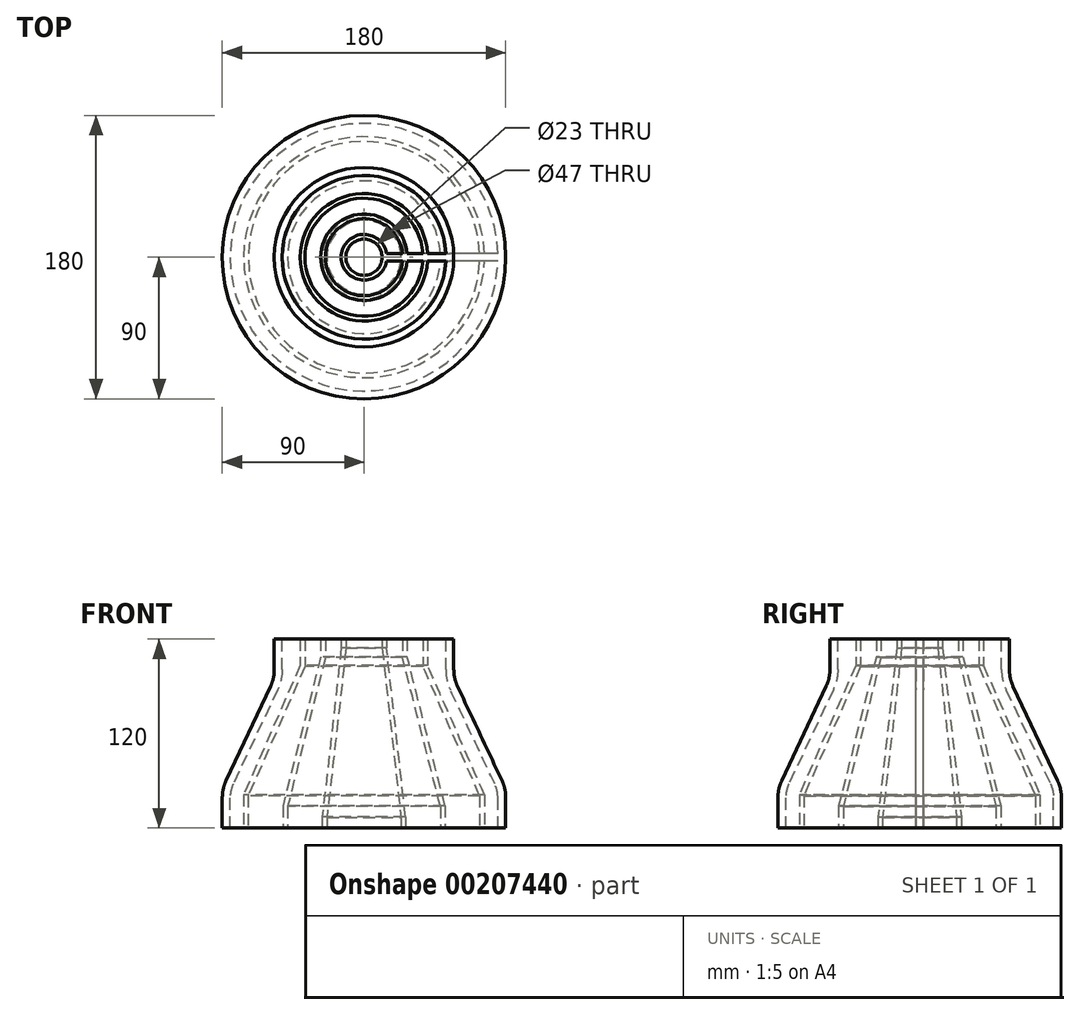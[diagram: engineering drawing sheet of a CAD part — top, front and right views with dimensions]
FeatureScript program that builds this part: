
annotation { "Feature Type Name" : "Feature", "Feature Type Description" : "" }
export const myFeature = defineFeature(function(context is Context, id is Id, definition is map)
    precondition{}
    {
        {
            var Q0;
            Q0=qCreatedBy(makeId("Front.planeOp"),FACE);
            var sketch = newSketch(context, id + "F0", { "sketchPlane" : qUnion([Q0])});
            skLineSegment(sketch, "E0", {"start": v(0, 0) * mm, "end": v(90, 0) * mm});
            skLineSegment(sketch, "E1", {"start": v(90, 0) * mm, "end": v(90, 19.4) * mm});
            skLineSegment(sketch, "E2", {"start": v(87.61, 30.06) * mm, "end": v(59.39, 89.94) * mm});
            skLineSegment(sketch, "E3", {"start": v(57, 100.6) * mm, "end": v(57, 120) * mm});
            skLineSegment(sketch, "E4", {"start": v(57, 120) * mm, "end": v(0, 120) * mm});
            skLineSegment(sketch, "E5", {"start": v(0, 120) * mm, "end": v(0, 0) * mm});
            skPoint(sketch, "E6.visualSharp", {"position": v(57, 95) * mm});
            skArc(sketch, "E6.filletArc", {"start": v(57, 100.6) * mm, "mid": v(57.6, 95.14) * mm, "end": v(59.39, 89.94) * mm});
            skPoint(sketch, "E7.visualSharp", {"position": v(90, 25) * mm});
            skArc(sketch, "E7.filletArc", {"start": v(90, 19.4) * mm, "mid": v(89.4, 24.86) * mm, "end": v(87.61, 30.06) * mm});
            skSolve(sketch);
        }
        {
            var Q0;
            Q0=makeQuery(id+"F0.imprint","IMPRINT",FACE,{"disambiguationData":[TD([[makeQuery(id+"F0.imprint","IMPRINT",EDGE,{"derivedFrom":sQuery(id+"F0.wireOp",EDGE,"E0")}),1.0]])]});
            var Q1;
            Q1=sQuery(id+"F0.wireOp",EDGE,"E5");
            revolve(context, id + "F1", {"entities" : qUnion([Q0]), "axis" : qUnion([Q1]), "revolveType" : RevolveType.FULL});
        }
        {
            var Q0;
            Q0=makeQuery(id+"F1.opRevolve","SWEPT_FACE",FACE,{"disambiguationData":[OSD([sQuery(id+"F0.wireOp",EDGE,"E4")])]});
            var Q1;
            Q1=makeQuery(id+"F1.opRevolve","SWEPT_FACE",FACE,{"disambiguationData":[OSD([sQuery(id+"F0.wireOp",EDGE,"E0")])]});
            shell(context, id + "F2", {"entities" : qUnion([Q0, Q1]), "thickness" : 5 * mm});
        }
        {
            var Q0;
            Q0=qCreatedBy(makeId("Front.planeOp"),FACE);
            var sketch = newSketch(context, id + "F3", { "sketchPlane" : qUnion([Q0])});
            skLineSegment(sketch, "E8", {"start": v(0, 0) * mm, "end": v(0, 120) * mm});
            skLineSegment(sketch, "E9", {"start": v(13, 120) * mm, "end": v(13, 114.3) * mm, "construction": true});
            skLineSegment(sketch, "E10", {"start": v(13, 114.3) * mm, "end": v(25, 6.94) * mm, "construction": true});
            skLineSegment(sketch, "E11", {"start": v(25, 6.94) * mm, "end": v(25, 0) * mm, "construction": true});
            skLineSegment(sketch, "E12", {"start": v(26, 120) * mm, "end": v(26, 108.6) * mm, "construction": true});
            skLineSegment(sketch, "E13", {"start": v(26, 108.6) * mm, "end": v(50, 13.89) * mm, "construction": true});
            skLineSegment(sketch, "E14", {"start": v(50, 13.89) * mm, "end": v(50, 0) * mm, "construction": true});
            skLineSegment(sketch, "E15", {"start": v(39, 120) * mm, "end": v(39, 102.9) * mm, "construction": true});
            skLineSegment(sketch, "E16", {"start": v(39, 102.9) * mm, "end": v(75, 20.83) * mm, "construction": true});
            skLineSegment(sketch, "E17", {"start": v(75, 20.83) * mm, "end": v(75, 0) * mm, "construction": true});
            skLineSegment(sketch, "E18", {"start": v(-57, 100.6) * mm, "end": v(-57, 120) * mm});
            skLineSegment(sketch, "E19", {"start": v(57, 120) * mm, "end": v(57, 100.6) * mm, "construction": true});
            skLineSegment(sketch, "E20", {"start": v(59.39, 89.94) * mm, "end": v(87.61, 30.06) * mm, "construction": true});
            skLineSegment(sketch, "E21", {"start": v(-87.61, 30.06) * mm, "end": v(-59.39, 89.94) * mm});
            skLineSegment(sketch, "E22", {"start": v(57, 100.6) * mm, "end": v(57, 95) * mm, "construction": true});
            skLineSegment(sketch, "E23", {"start": v(59.39, 89.94) * mm, "end": v(57, 95) * mm, "construction": true});
            skLineSegment(sketch, "E24", {"start": v(0, 120) * mm, "end": v(57, 95) * mm, "construction": true});
            skLineSegment(sketch, "E25", {"start": v(90, 19.1) * mm, "end": v(90, 0) * mm, "construction": true});
            skLineSegment(sketch, "E26", {"start": v(87.61, 30.06) * mm, "end": v(90, 25) * mm, "construction": true});
            skLineSegment(sketch, "E27", {"start": v(90, 19.1) * mm, "end": v(90, 25) * mm, "construction": true});
            skLineSegment(sketch, "E28", {"start": v(0, 0) * mm, "end": v(90, 25) * mm, "construction": true});
            skLineSegment(sketch, "E29.0", {"start": v(23.5, 6.86) * mm, "end": v(23.5, 0) * mm});
            skLineSegment(sketch, "E29.1", {"start": v(11.5, 114.21) * mm, "end": v(23.5, 6.86) * mm});
            skLineSegment(sketch, "E29.2", {"start": v(11.5, 120) * mm, "end": v(11.5, 114.21) * mm});
            skLineSegment(sketch, "E30.0", {"start": v(26.5, 7.03) * mm, "end": v(26.5, 0) * mm});
            skLineSegment(sketch, "E30.1", {"start": v(14.5, 114.38) * mm, "end": v(26.5, 7.03) * mm});
            skLineSegment(sketch, "E30.2", {"start": v(14.5, 120) * mm, "end": v(14.5, 114.38) * mm});
            skLineSegment(sketch, "E31.0", {"start": v(48.5, 13.7) * mm, "end": v(48.5, 0) * mm});
            skLineSegment(sketch, "E31.1", {"start": v(24.5, 108.4) * mm, "end": v(48.5, 13.7) * mm});
            skLineSegment(sketch, "E31.2", {"start": v(24.5, 120) * mm, "end": v(24.5, 108.4) * mm});
            skLineSegment(sketch, "E32.0", {"start": v(51.5, 14.08) * mm, "end": v(51.5, 0) * mm});
            skLineSegment(sketch, "E32.1", {"start": v(27.5, 108.78) * mm, "end": v(51.5, 14.08) * mm});
            skLineSegment(sketch, "E32.2", {"start": v(27.5, 120) * mm, "end": v(27.5, 108.78) * mm});
            skLineSegment(sketch, "E33.0", {"start": v(73.5, 20.52) * mm, "end": v(73.5, 0) * mm});
            skLineSegment(sketch, "E33.1", {"start": v(37.5, 102.58) * mm, "end": v(73.5, 20.52) * mm});
            skLineSegment(sketch, "E33.2", {"start": v(37.5, 120) * mm, "end": v(37.5, 102.58) * mm});
            skLineSegment(sketch, "E34.0", {"start": v(76.5, 21.15) * mm, "end": v(76.5, 0) * mm});
            skLineSegment(sketch, "E34.1", {"start": v(40.5, 103.2) * mm, "end": v(76.5, 21.15) * mm});
            skLineSegment(sketch, "E34.2", {"start": v(40.5, 120) * mm, "end": v(40.5, 103.2) * mm});
            skLineSegment(sketch, "E35", {"start": v(11.5, 120) * mm, "end": v(14.5, 120) * mm});
            skLineSegment(sketch, "E36", {"start": v(24.5, 120) * mm, "end": v(27.5, 120) * mm});
            skLineSegment(sketch, "E37", {"start": v(37.5, 120) * mm, "end": v(40.5, 120) * mm});
            skLineSegment(sketch, "E38", {"start": v(23.5, 0) * mm, "end": v(26.5, 0) * mm});
            skLineSegment(sketch, "E39", {"start": v(48.5, 0) * mm, "end": v(51.5, 0) * mm});
            skLineSegment(sketch, "E40", {"start": v(73.5, 0) * mm, "end": v(76.5, 0) * mm});
            skSolve(sketch);
        }
        {
            var Q0;
            Q0=makeQuery(id+"F3.imprint","IMPRINT",FACE,{"disambiguationData":[TD([[makeQuery(id+"F3.imprint","IMPRINT",EDGE,{"derivedFrom":sQuery(id+"F3.wireOp",EDGE,"E29.0")}),1.0]])]});
            var Q1;
            Q1=makeQuery(id+"F3.imprint","IMPRINT",FACE,{"disambiguationData":[TD([[makeQuery(id+"F3.imprint","IMPRINT",EDGE,{"derivedFrom":sQuery(id+"F3.wireOp",EDGE,"E33.0")}),1.0]])]});
            var Q2;
            Q2=makeQuery(id+"F3.imprint","IMPRINT",FACE,{"disambiguationData":[TD([[makeQuery(id+"F3.imprint","IMPRINT",EDGE,{"derivedFrom":sQuery(id+"F3.wireOp",EDGE,"E31.0")}),1.0]])]});
            var Q3;
            Q3=sQuery(id+"F3.wireOp",EDGE,"E8");
            revolve(context, id + "F4", {"entities" : qUnion([Q0, Q1, Q2]), "axis" : qUnion([Q3]), "revolveType" : RevolveType.FULL});
        }
        {
            var Q0;
            Q0=qCreatedBy(makeId("Front.planeOp"),FACE);
            var sketch = newSketch(context, id + "F5", { "sketchPlane" : qUnion([Q0])});
            skLineSegment(sketch, "E41", {"start": v(25.18, 0) * mm, "end": v(25.18, 13.29) * mm});
            skLineSegment(sketch, "E42", {"start": v(25.18, 13.29) * mm, "end": v(12, 113.7) * mm});
            skLineSegment(sketch, "E43", {"start": v(12, 113.7) * mm, "end": v(12, 120) * mm});
            skLineSegment(sketch, "E44", {"start": v(12, 120) * mm, "end": v(54.1, 120) * mm});
            skLineSegment(sketch, "E45", {"start": v(54.1, 120) * mm, "end": v(54.1, 94.33) * mm});
            skLineSegment(sketch, "E46", {"start": v(54.1, 94.33) * mm, "end": v(88, 26.19) * mm});
            skLineSegment(sketch, "E47", {"start": v(88, 26.19) * mm, "end": v(88, 0) * mm});
            skLineSegment(sketch, "E48", {"start": v(88, 0) * mm, "end": v(25.18, 0) * mm});
            skPoint(sketch, "E49.end.orphan", {"position": v(90, 0) * mm});
            skSolve(sketch);
        }
        {
            var Q0;
            Q0 = qSketchRegion(id + "F5", true);
            extrude(context, id + "F6", {"entities" : qUnion([Q0]), "operationType" : NewBodyOperationType.ADD, "depth" : 2.5 * mm, "hasSecondDirection" : true, "secondDirectionOppositeDirection" : true, "secondDirectionDepth" : 2.5 * mm});
        }
    });
